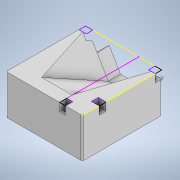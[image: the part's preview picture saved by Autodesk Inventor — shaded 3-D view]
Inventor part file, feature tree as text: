
AUTODESK INVENTOR PART (.ipt)
format: ipt  version: 2020 (Build 240168000, 168)  size: 200,704 bytes
history: native  units: in
note: dims shown in document units (in); Inventor stores cm internally (conversion verified against a paired STEP export)
features: sketch x6, extrude x4, hole x1, sweep x1
ambient origin geometry x8: Origin, YZ Plane, XZ Plane, XY Plane, X Axis, Y Axis, Z Axis, Center Point
bodies: Solid1 (feature_tree)
feature tree (12):
  extrude  "Extrusion1"  Depth=6.5in
  hole  "Hole1"  [1 undecoded]
  sweep  "Sweep1"
  sketch  "Sketch9"  dims[d9=0.3125in d10=5.5625in]
  extrude  "Extrusion2"  Depth=3.25in
  extrude  "Extrusion3"  Depth=5.5625in
  extrude  "Extrusion5"  Depth=1.0in
  sketch  "Sketch1"  dims[d0=6.25in d1=6.5in]
  sketch  "Sketch2"  dims[d2=0.125in d3=0.125in]
  sketch  "Sketch7"  dims[d4=0.125in d5=0.125in]
  sketch  "Sketch8"  dims[d6=3.25in d7=0.0in d8=0.3125in]
  sketch  "Sketch11"  dims[d11=4.5625in d12=1.9291in d13=135.0deg d14=0.1875in d15=0.75in d16=0.375in d17=0.25in d18=0.5635in d19=1.0in d20=0.8108in d22=1.75in d23=0.0in d24=2.5in d25=3.0in d27=0.0in d28=0.0in d29=0.65in d30=0.0in d31=3.15in d32=0.0in d40=0.125in d41=0.125in d42=0.125in d43=1.0in d44=0.0in]
note: 1 required parameter value undecoded (feature->parameter linkage not recoverable at this tier; creation-order binding heuristic only, values carry confidence <= 0.55)
